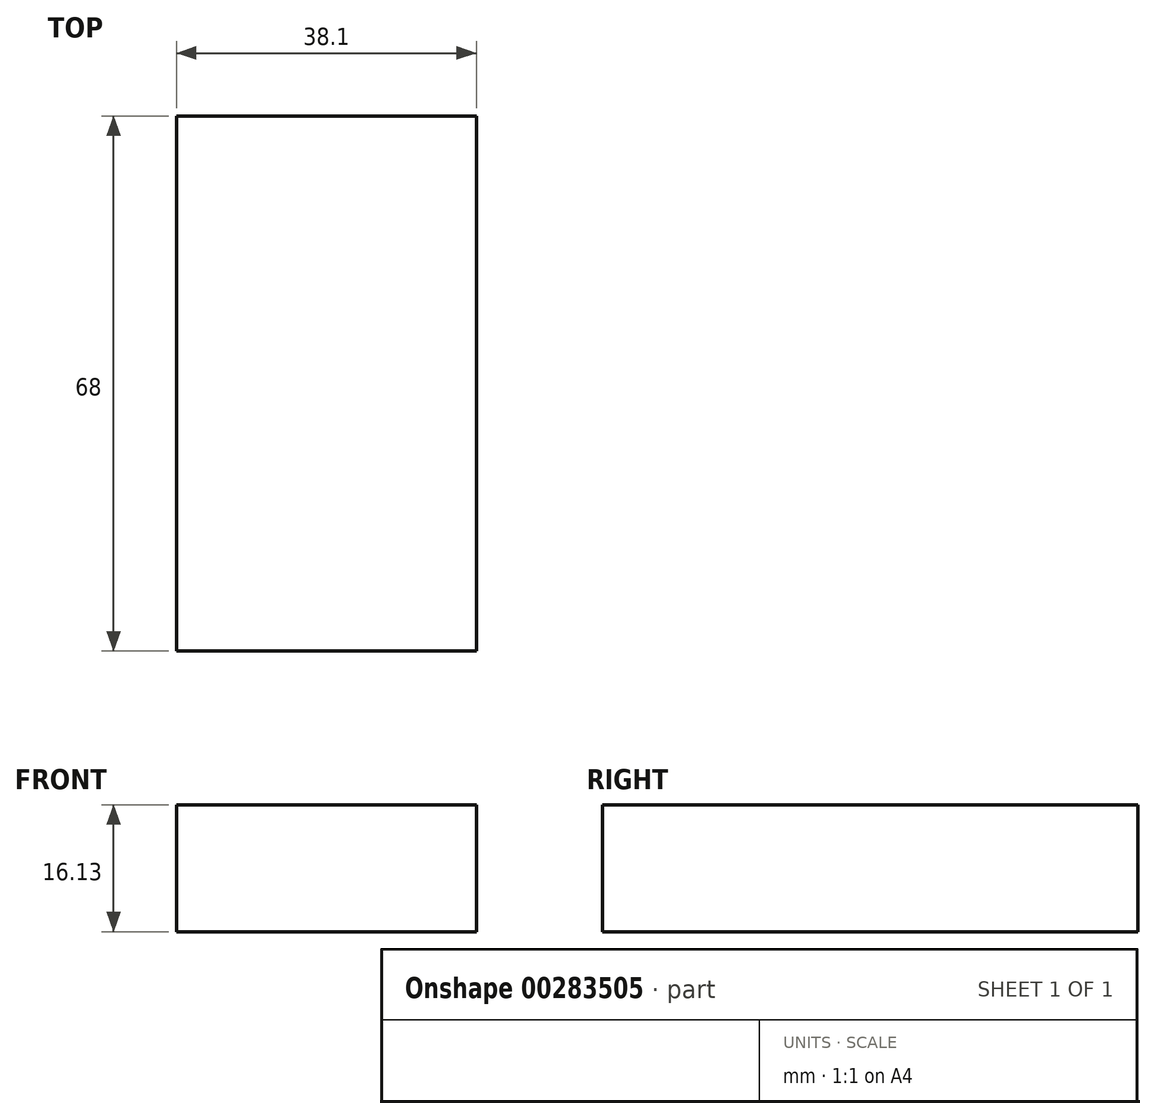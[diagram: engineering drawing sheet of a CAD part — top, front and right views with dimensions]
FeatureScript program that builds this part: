
annotation { "Feature Type Name" : "Feature", "Feature Type Description" : "" }
export const myFeature = defineFeature(function(context is Context, id is Id, definition is map)
    precondition{}
    {
        {
            var Q0;
            Q0=qCreatedBy(makeId("Right.planeOp"),FACE);
            var sketch = newSketch(context, id + "F0", { "sketchPlane" : qUnion([Q0])});
            skLineSegment(sketch, "E0.bottom", {"start": v(21.19, -16.13) * mm, "end": v(-46.8, -16.13) * mm});
            skLineSegment(sketch, "E0.top", {"start": v(21.19, 0) * mm, "end": v(-46.8, 0) * mm});
            skLineSegment(sketch, "E0.left", {"start": v(21.19, -16.13) * mm, "end": v(21.19, 0) * mm});
            skLineSegment(sketch, "E0.right", {"start": v(-46.8, -16.13) * mm, "end": v(-46.8, 0) * mm});
            skLineSegment(sketch, "E1.bottom", {"start": v(-24.67, 0) * mm, "end": v(-46.8, 0) * mm});
            skLineSegment(sketch, "E1.top", {"start": v(-24.67, 21.19) * mm, "end": v(-46.8, 21.19) * mm});
            skLineSegment(sketch, "E1.left", {"start": v(-24.67, 0) * mm, "end": v(-24.67, 21.19) * mm});
            skLineSegment(sketch, "E1.right", {"start": v(-46.8, 0) * mm, "end": v(-46.8, 21.19) * mm});
            skLineSegment(sketch, "E2.bottom", {"start": v(-31, 21.19) * mm, "end": v(-35.42, 21.19) * mm});
            skLineSegment(sketch, "E2.top", {"start": v(-31, 27.51) * mm, "end": v(-35.42, 27.51) * mm});
            skLineSegment(sketch, "E2.left", {"start": v(-31, 21.19) * mm, "end": v(-31, 27.51) * mm});
            skLineSegment(sketch, "E2.right", {"start": v(-35.42, 21.19) * mm, "end": v(-35.42, 27.51) * mm});
            skLineSegment(sketch, "E3.bottom", {"start": v(-29.73, -16.13) * mm, "end": v(-40.16, -16.13) * mm});
            skLineSegment(sketch, "E3.top", {"start": v(-29.73, -27.83) * mm, "end": v(-40.16, -27.83) * mm});
            skLineSegment(sketch, "E3.left", {"start": v(-29.73, -16.13) * mm, "end": v(-29.73, -27.83) * mm});
            skLineSegment(sketch, "E3.right", {"start": v(-40.16, -16.13) * mm, "end": v(-40.16, -27.83) * mm});
            skPoint(sketch, "E4.oppositeSnap0", {"position": v(-34.95, -27.83) * mm});
            skLineSegment(sketch, "E4.bottom", {"start": v(0, -16.13) * mm, "end": v(8.86, -16.13) * mm});
            skLineSegment(sketch, "E4.top", {"start": v(0, -27.83) * mm, "end": v(8.86, -27.83) * mm});
            skLineSegment(sketch, "E4.left", {"start": v(0, -16.13) * mm, "end": v(0, -27.83) * mm});
            skLineSegment(sketch, "E4.right", {"start": v(8.86, -16.13) * mm, "end": v(8.86, -27.83) * mm});
            skLineSegment(sketch, "E5.bottom", {"start": v(13.28, 0) * mm, "end": v(-19.6, 0) * mm});
            skLineSegment(sketch, "E5.top", {"start": v(13.28, 21.19) * mm, "end": v(-19.6, 21.19) * mm});
            skLineSegment(sketch, "E5.left", {"start": v(13.28, 0) * mm, "end": v(13.28, 21.19) * mm});
            skLineSegment(sketch, "E5.right", {"start": v(-19.6, 0) * mm, "end": v(-19.6, 21.19) * mm});
            skLineSegment(sketch, "E6.bottom", {"start": v(6.96, 21.19) * mm, "end": v(-14.55, 21.19) * mm});
            skLineSegment(sketch, "E6.top", {"start": v(6.96, 24.66) * mm, "end": v(-14.55, 24.66) * mm});
            skLineSegment(sketch, "E6.left", {"start": v(6.96, 21.19) * mm, "end": v(6.96, 24.66) * mm});
            skLineSegment(sketch, "E6.right", {"start": v(-14.55, 21.19) * mm, "end": v(-14.55, 24.66) * mm});
            skLineSegment(sketch, "E7.bottom", {"start": v(0, 24.66) * mm, "end": v(-8.86, 24.66) * mm});
            skLineSegment(sketch, "E7.top", {"start": v(0, 27.51) * mm, "end": v(-8.86, 27.51) * mm});
            skLineSegment(sketch, "E7.left", {"start": v(0, 24.66) * mm, "end": v(0, 27.51) * mm});
            skLineSegment(sketch, "E7.right", {"start": v(-8.86, 24.66) * mm, "end": v(-8.86, 27.51) * mm});
            skSolve(sketch);
        }
        {
            var Q0;
            Q0=makeQuery(id+"F0.imprint","IMPRINT",FACE,{"disambiguationData":[TD([[makeQuery(id+"F0.imprint","IMPRINT",EDGE,{"derivedFrom":sQuery(id+"F0.wireOp",EDGE,"E6.bottom")}),-1.0]])]});
            var Q1;
            Q1=makeQuery(id+"F0.imprint","IMPRINT",FACE,{"disambiguationData":[TD([[makeQuery(id+"F0.imprint","IMPRINT",EDGE,{"derivedFrom":sQuery(id+"F0.wireOp",EDGE,"E7.bottom")}),-1.0]])]});
            var Q2;
            Q2=makeQuery(id+"F0.imprint","IMPRINT",FACE,{"disambiguationData":[TD([[makeQuery(id+"F0.imprint","IMPRINT",EDGE,{"derivedFrom":sQuery(id+"F0.wireOp",EDGE,"E5.bottom")}),-1.0]])]});
            var Q3;
            {var subQ4=sQuery(id+"F0.wireOp",EDGE,"E0.left");Q3=makeQuery(id+"F0.imprint","IMPRINT",FACE,{"disambiguationData":[TD([[makeQuery(id+"F0.imprint","IMPRINT",EDGE,{"derivedFrom":subQ4}),1.0]])]});}
            var Q4;
            Q4=makeQuery(id+"F0.imprint","IMPRINT",FACE,{"disambiguationData":[TD([[makeQuery(id+"F0.imprint","IMPRINT",EDGE,{"derivedFrom":sQuery(id+"F0.wireOp",EDGE,"E1.bottom")}),-1.0]])]});
            var Q5;
            Q5=makeQuery(id+"F0.imprint","IMPRINT",FACE,{"disambiguationData":[TD([[makeQuery(id+"F0.imprint","IMPRINT",EDGE,{"derivedFrom":sQuery(id+"F0.wireOp",EDGE,"E2.bottom")}),-1.0]])]});
            var Q6;
            Q6=makeQuery(id+"F0.imprint","IMPRINT",FACE,{"disambiguationData":[TD([[makeQuery(id+"F0.imprint","IMPRINT",EDGE,{"derivedFrom":sQuery(id+"F0.wireOp",EDGE,"E4.bottom")}),-1.0]])]});
            var Q7;
            Q7=makeQuery(id+"F0.imprint","IMPRINT",FACE,{"disambiguationData":[TD([[makeQuery(id+"F0.imprint","IMPRINT",EDGE,{"derivedFrom":sQuery(id+"F0.wireOp",EDGE,"E3.bottom")}),1.0]])]});
            extrude(context, id + "F1", {"entities" : qUnion([Q0, Q1, Q2, Q3, Q4, Q5, Q6, Q7]), "depth" : 38.1 * mm});
        }
    });
